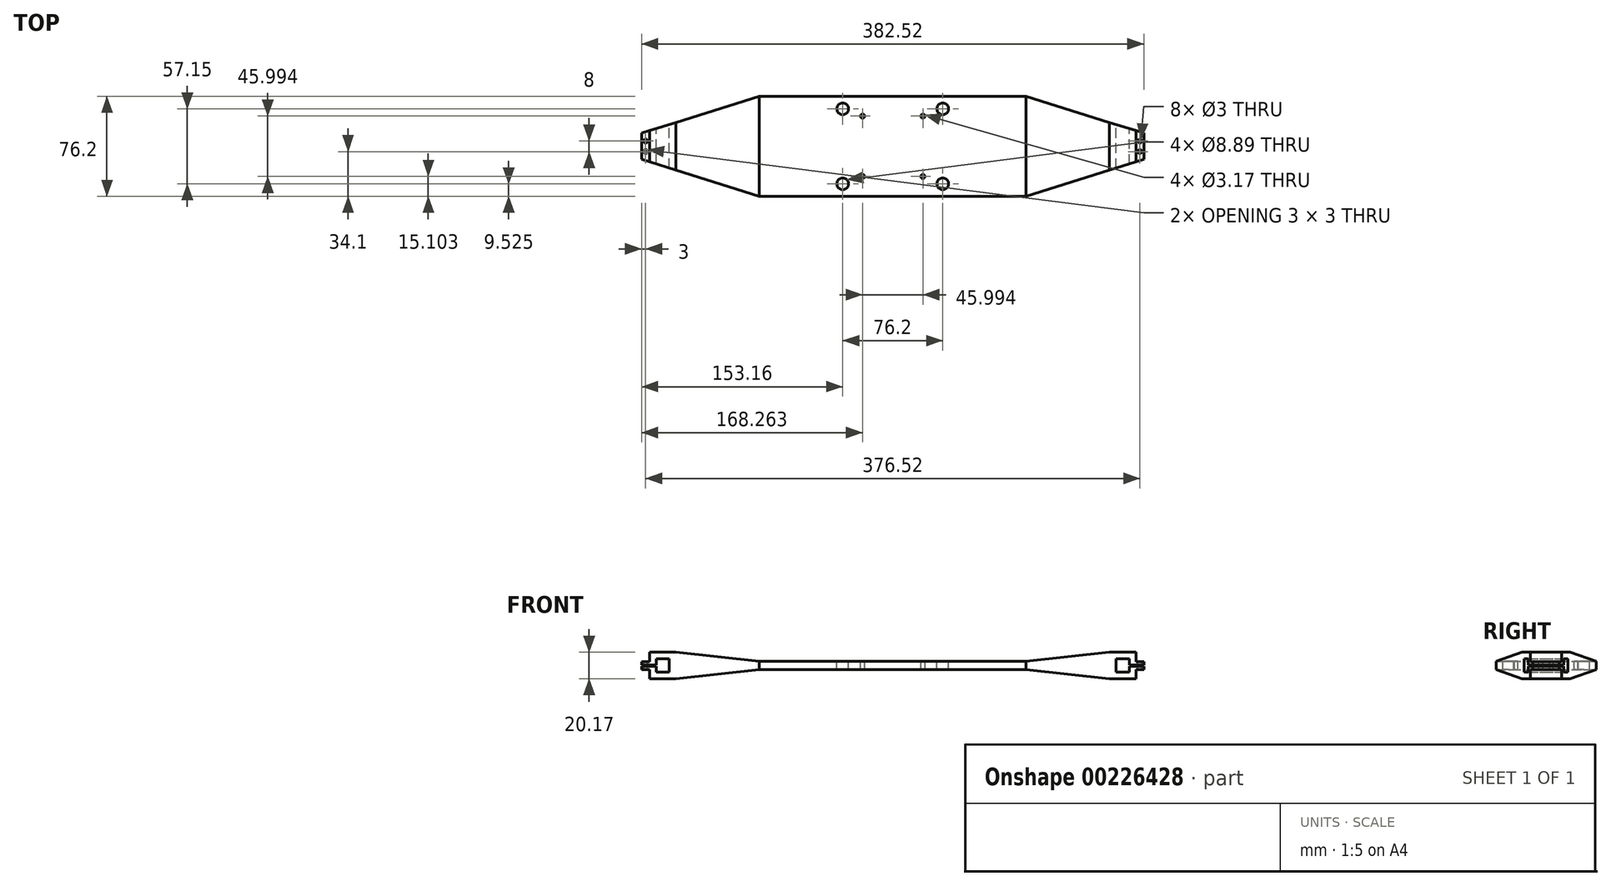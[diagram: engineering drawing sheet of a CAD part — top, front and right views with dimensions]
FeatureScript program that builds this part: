
annotation { "Feature Type Name" : "Feature", "Feature Type Description" : "" }
export const myFeature = defineFeature(function(context is Context, id is Id, definition is map)
    precondition{}
    {
        {
            var Q0;
            Q0=qCreatedBy(makeId("Front.planeOp"),FACE);
            var sketch = newSketch(context, id + "F0", { "sketchPlane" : qUnion([Q0])});
            skLineSegment(sketch, "E0.bottom", {"start": v(-180.18, 8.18) * mm, "end": v(-170.18, 8.18) * mm});
            skLineSegment(sketch, "E0.top", {"start": v(-180.18, -1.83) * mm, "end": v(-170.18, -1.83) * mm});
            skLineSegment(sketch, "E0.right", {"start": v(-170.18, 8.18) * mm, "end": v(-170.18, -1.83) * mm});
            skLineSegment(sketch, "E1.bottom", {"start": v(-165.1, -6.9) * mm, "end": v(-185.26, -6.9) * mm});
            skLineSegment(sketch, "E1.top", {"start": v(-165.1, 13.25) * mm, "end": v(-185.26, 13.25) * mm});
            skLineSegment(sketch, "E1.left", {"start": v(-165.1, -6.9) * mm, "end": v(-165.1, 13.25) * mm});
            skLineSegment(sketch, "E1.right", {"start": v(-185.26, -6.9) * mm, "end": v(-185.26, 2.68) * mm});
            skPoint(sketch, "E1.middle", {"position": v(-175.18, 3.17) * mm});
            skLineSegment(sketch, "E2", {"start": v(-185.26, 13.25) * mm, "end": v(-180.18, 8.17) * mm, "construction": true});
            skLineSegment(sketch, "E3", {"start": v(-170.18, -1.83) * mm, "end": v(-165.1, -6.9) * mm, "construction": true});
            skLineSegment(sketch, "E4", {"start": v(-180.18, -1.82) * mm, "end": v(-185.26, -6.9) * mm, "construction": true});
            skLineSegment(sketch, "E5", {"start": v(-165.1, 6.35) * mm, "end": v(0, 6.35) * mm});
            skLineSegment(sketch, "E6", {"start": v(0, 0) * mm, "end": v(-165.1, 0) * mm});
            skLineSegment(sketch, "E7", {"start": v(-165.1, 13.25) * mm, "end": v(-101.6, 6.35) * mm});
            skLineSegment(sketch, "E8", {"start": v(-101.6, 6.35) * mm, "end": v(-101.6, 0) * mm});
            skLineSegment(sketch, "E9", {"start": v(-101.6, 0) * mm, "end": v(-165.1, -6.9) * mm});
            skLineSegment(sketch, "E10", {"start": v(0, 6.35) * mm, "end": v(0, 0) * mm});
            skLineSegment(sketch, "E11", {"start": v(-180.18, 3.68) * mm, "end": v(-185.26, 3.68) * mm});
            skLineSegment(sketch, "E12", {"start": v(-185.26, 2.68) * mm, "end": v(-180.18, 2.68) * mm});
            skPoint(sketch, "E13", {"position": v(-180.18, 3.17) * mm});
            skLineSegment(sketch, "E14.trimOffspring", {"start": v(-180.18, 2.68) * mm, "end": v(-180.18, -1.83) * mm});
            skLineSegment(sketch, "E15", {"start": v(-180.18, 3.67) * mm, "end": v(-180.18, 8.17) * mm});
            skLineSegment(sketch, "E16.trimOffspring", {"start": v(-185.26, 3.67) * mm, "end": v(-185.26, 13.25) * mm});
            skLineSegment(sketch, "E17", {"start": v(-185.26, 3.68) * mm, "end": v(-191.26, 3.68) * mm});
            skLineSegment(sketch, "E18", {"start": v(-191.26, 3.67) * mm, "end": v(-191.26, 6.22) * mm});
            skLineSegment(sketch, "E19", {"start": v(-191.26, 6.22) * mm, "end": v(-185.26, 6.22) * mm});
            skLineSegment(sketch, "E20", {"start": v(-185.26, 2.68) * mm, "end": v(-191.26, 2.68) * mm});
            skLineSegment(sketch, "E21", {"start": v(-191.26, 2.68) * mm, "end": v(-191.26, 0.13) * mm});
            skLineSegment(sketch, "E22", {"start": v(-191.26, 0.13) * mm, "end": v(-185.26, 0.13) * mm});
            skLineSegment(sketch, "E23.MirrorCS", {"start": v(180.18, 3.67) * mm, "end": v(180.18, 8.17) * mm});
            skLineSegment(sketch, "E24.MirrorCS", {"start": v(180.18, 2.68) * mm, "end": v(180.18, -1.83) * mm});
            skLineSegment(sketch, "E25.MirrorCS", {"start": v(191.26, 3.67) * mm, "end": v(191.26, 6.22) * mm});
            skLineSegment(sketch, "E26.MirrorCS", {"start": v(191.26, 2.67) * mm, "end": v(191.26, 0.13) * mm});
            skLineSegment(sketch, "E27.MirrorCS", {"start": v(180.18, 8.18) * mm, "end": v(170.18, 8.18) * mm});
            skLineSegment(sketch, "E28.MirrorCS", {"start": v(180.18, 3.68) * mm, "end": v(185.26, 3.68) * mm});
            skLineSegment(sketch, "E29.MirrorCS", {"start": v(185.26, 2.68) * mm, "end": v(180.18, 2.68) * mm});
            skLineSegment(sketch, "E30.MirrorCS", {"start": v(180.18, -1.82) * mm, "end": v(185.26, -6.9) * mm, "construction": true});
            skLineSegment(sketch, "E31.MirrorCS", {"start": v(185.26, 13.25) * mm, "end": v(180.18, 8.17) * mm, "construction": true});
            skLineSegment(sketch, "E32.MirrorCS", {"start": v(191.26, 6.22) * mm, "end": v(185.26, 6.22) * mm});
            skLineSegment(sketch, "E33.MirrorCS", {"start": v(185.26, -6.9) * mm, "end": v(185.26, 2.68) * mm});
            skLineSegment(sketch, "E34.MirrorCS", {"start": v(191.26, 0.13) * mm, "end": v(185.26, 0.13) * mm});
            skLineSegment(sketch, "E35.MirrorCS", {"start": v(170.18, 8.18) * mm, "end": v(170.18, -1.82) * mm});
            skLineSegment(sketch, "E36.MirrorCS", {"start": v(0, 0) * mm, "end": v(165.1, 0) * mm});
            skLineSegment(sketch, "E37.MirrorCS", {"start": v(180.18, -1.83) * mm, "end": v(170.18, -1.83) * mm});
            skPoint(sketch, "E38.MirrorP", {"position": v(175.18, 3.17) * mm});
            skPoint(sketch, "E39.MirrorP", {"position": v(180.18, 3.17) * mm});
            skLineSegment(sketch, "E40.MirrorCS", {"start": v(101.6, 6.35) * mm, "end": v(101.6, 0) * mm});
            skLineSegment(sketch, "E41.MirrorCS", {"start": v(165.1, 13.25) * mm, "end": v(185.26, 13.25) * mm});
            skLineSegment(sketch, "E42.MirrorCS", {"start": v(165.1, -6.9) * mm, "end": v(185.26, -6.9) * mm});
            skLineSegment(sketch, "E43.MirrorCS", {"start": v(185.26, 3.67) * mm, "end": v(185.26, 13.25) * mm});
            skLineSegment(sketch, "E44.MirrorCS", {"start": v(165.1, -6.9) * mm, "end": v(165.1, 13.25) * mm});
            skLineSegment(sketch, "E45.MirrorCS", {"start": v(165.1, 6.35) * mm, "end": v(0, 6.35) * mm});
            skLineSegment(sketch, "E46.MirrorCS", {"start": v(185.26, 3.68) * mm, "end": v(191.26, 3.68) * mm});
            skLineSegment(sketch, "E47.MirrorCS", {"start": v(101.6, 0) * mm, "end": v(165.1, -6.9) * mm});
            skLineSegment(sketch, "E48.MirrorCS", {"start": v(185.26, 2.68) * mm, "end": v(191.26, 2.68) * mm});
            skLineSegment(sketch, "E49.MirrorCS", {"start": v(170.18, -1.83) * mm, "end": v(165.1, -6.9) * mm, "construction": true});
            skLineSegment(sketch, "E50.MirrorCS", {"start": v(165.1, 13.25) * mm, "end": v(101.6, 6.35) * mm});
            skSolve(sketch);
        }
        {
            var Q0;
            Q0 = qSketchRegion(id + "F0", true);
            extrude(context, id + "F1", {"entities" : qUnion([Q0]), "depth" : 76.2 * mm, "offsetDistance" : 25.4 * mm});
        }
        {
            var Q0;
            Q0=makeQuery(id+"F1.opExtrude","SWEPT_FACE",FACE,{"disambiguationData":[OSD([sQuery(id+"F0.wireOp",EDGE,"E5")])]});
            var sketch = newSketch(context, id + "F2", { "sketchPlane" : qUnion([Q0])});
            skLineSegment(sketch, "E51.bottom", {"start": v(-101.6, 0) * mm, "end": v(101.6, 0) * mm, "construction": true});
            skLineSegment(sketch, "E51.top", {"start": v(-101.6, -76.2) * mm, "end": v(101.6, -76.2) * mm, "construction": true});
            skLineSegment(sketch, "E51.left", {"start": v(-101.6, 0) * mm, "end": v(-101.6, -76.2) * mm, "construction": true});
            skLineSegment(sketch, "E51.right", {"start": v(101.6, 0) * mm, "end": v(101.6, -76.2) * mm, "construction": true});
            skLineSegment(sketch, "E52.bottom", {"start": v(-26, -12.1) * mm, "end": v(26, -12.1) * mm, "construction": true});
            skLineSegment(sketch, "E52.top", {"start": v(-26, -64.1) * mm, "end": v(26, -64.1) * mm, "construction": true});
            skLineSegment(sketch, "E52.left", {"start": v(-26, -12.1) * mm, "end": v(-26, -64.1) * mm, "construction": true});
            skLineSegment(sketch, "E52.right", {"start": v(26, -12.1) * mm, "end": v(26, -64.1) * mm, "construction": true});
            skLineSegment(sketch, "E53.bottom", {"start": v(-38.1, -9.52) * mm, "end": v(38.1, -9.52) * mm, "construction": true});
            skLineSegment(sketch, "E53.top", {"start": v(-38.1, -66.68) * mm, "end": v(38.1, -66.68) * mm, "construction": true});
            skLineSegment(sketch, "E53.left", {"start": v(-38.1, -9.52) * mm, "end": v(-38.1, -66.67) * mm, "construction": true});
            skLineSegment(sketch, "E53.right", {"start": v(38.1, -9.52) * mm, "end": v(38.1, -66.67) * mm, "construction": true});
            skLineSegment(sketch, "E54", {"start": v(0, -12.1) * mm, "end": v(0, 0) * mm, "construction": true});
            skLineSegment(sketch, "E55", {"start": v(26, -38.1) * mm, "end": v(101.6, -38.1) * mm, "construction": true});
            skLineSegment(sketch, "E56", {"start": v(0, -9.52) * mm, "end": v(0, 0) * mm});
            skLineSegment(sketch, "E57", {"start": v(38.1, -38.1) * mm, "end": v(101.6, -38.1) * mm, "construction": true});
            skCircle(sketch, "E58", {"center": v(-38.1, -9.52) * mm, "radius": 4.45 * mm});
            skCircle(sketch, "E59", {"center": v(38.1, -9.52) * mm, "radius": 4.45 * mm});
            skCircle(sketch, "E60", {"center": v(38.1, -66.67) * mm, "radius": 4.45 * mm});
            skCircle(sketch, "E61", {"center": v(-38.1, -66.67) * mm, "radius": 4.45 * mm});
            skCircle(sketch, "E62", {"center": v(-23, -15.1) * mm, "radius": 1.59 * mm});
            skCircle(sketch, "E63", {"center": v(23, -61.1) * mm, "radius": 1.59 * mm});
            skLineSegment(sketch, "E64", {"start": v(-23, -12.1) * mm, "end": v(-23, -64.1) * mm, "construction": true});
            skLineSegment(sketch, "E65", {"start": v(-26, -61.1) * mm, "end": v(26, -61.1) * mm, "construction": true});
            skLineSegment(sketch, "E66", {"start": v(23, -64.1) * mm, "end": v(23, -12.1) * mm, "construction": true});
            skLineSegment(sketch, "E67", {"start": v(26, -15.1) * mm, "end": v(-26, -15.1) * mm, "construction": true});
            skCircle(sketch, "E68", {"center": v(23, -15.1) * mm, "radius": 1.59 * mm});
            skCircle(sketch, "E69", {"center": v(-23, -61.1) * mm, "radius": 1.59 * mm});
            skSolve(sketch);
        }
        {
            var Q0;
            Q0 = qSketchRegion(id + "F2", true);
            extrude(context, id + "F3", {"entities" : qUnion([Q0]), "operationType" : NewBodyOperationType.REMOVE, "oppositeDirection" : true, "depth" : 25.4 * mm, "offsetDistance" : 25.4 * mm});
        }
        {
            var Q0;
            Q0=makeQuery(id+"F1.opExtrude","SWEPT_FACE",FACE,{"disambiguationData":[OSD([sQuery(id+"F0.wireOp",EDGE,"E19")])]});
            var sketch = newSketch(context, id + "F4", { "sketchPlane" : qUnion([Q0])});
            skCircle(sketch, "E70", {"center": v(-188.26, -34.1) * mm, "radius": 1.5 * mm});
            skPoint(sketch, "E70.centerSnap0", {"position": v(-188.26, 0) * mm});
            skCircle(sketch, "E71", {"center": v(-188.26, -42.1) * mm, "radius": 1.5 * mm});
            skPoint(sketch, "E71.centerSnap0", {"position": v(-188.26, -76.2) * mm});
            skLineSegment(sketch, "E72", {"start": v(0, 0) * mm, "end": v(0, -76.82) * mm});
            skCircle(sketch, "E73.MirrorC", {"center": v(188.26, -42.1) * mm, "radius": 1.5 * mm});
            skCircle(sketch, "E74.MirrorC", {"center": v(188.26, -34.1) * mm, "radius": 1.5 * mm});
            skPoint(sketch, "E75.MirrorP", {"position": v(188.26, -76.2) * mm});
            skSolve(sketch);
        }
        {
            var Q0;
            Q0 = qSketchRegion(id + "F4", true);
            extrude(context, id + "F5", {"entities" : qUnion([Q0]), "operationType" : NewBodyOperationType.REMOVE, "endBound" : BoundingType.THROUGH_ALL, "oppositeDirection" : true, "depth" : 25 * mm, "offsetDistance" : 25 * mm});
        }
        {
            var Q0;
            Q0=makeQuery(id+"F1.opExtrude","SWEPT_FACE",FACE,{"disambiguationData":[OSD([sQuery(id+"F0.wireOp",EDGE,"E1.top")])]});
            var sketch = newSketch(context, id + "F6", { "sketchPlane" : qUnion([Q0])});
            skPoint(sketch, "E76.0", {"position": v(-101.6, 0) * mm});
            skLineSegment(sketch, "E77", {"start": v(-101.6, 0) * mm, "end": v(-191.26, -28.1) * mm});
            skLineSegment(sketch, "E78.0", {"start": v(-191.26, -76.2) * mm, "end": v(-191.26, 0) * mm});
            skPoint(sketch, "E79", {"position": v(-191.26, -38.1) * mm});
            skLineSegment(sketch, "E80.MirrorCS", {"start": v(101.6, 0) * mm, "end": v(191.26, -28.1) * mm});
            skLineSegment(sketch, "E81", {"start": v(-191.26, -38.1) * mm, "end": v(196.24, -38.1) * mm});
            skLineSegment(sketch, "E82.MirrorCS", {"start": v(-101.6, -76.2) * mm, "end": v(-191.26, -48.1) * mm});
            skLineSegment(sketch, "E83.MirrorCS", {"start": v(101.6, -76.2) * mm, "end": v(191.26, -48.1) * mm});
            skLineSegment(sketch, "E84", {"start": v(-101.6, 0) * mm, "end": v(-191.26, 0) * mm});
            skLineSegment(sketch, "E85", {"start": v(-101.6, -76.2) * mm, "end": v(-191.26, -76.2) * mm});
            skLineSegment(sketch, "E86", {"start": v(101.6, -76.2) * mm, "end": v(191.26, -76.2) * mm});
            skLineSegment(sketch, "E87", {"start": v(191.26, -76.2) * mm, "end": v(191.26, -48.1) * mm});
            skLineSegment(sketch, "E88", {"start": v(191.26, -28.1) * mm, "end": v(191.26, 0) * mm});
            skLineSegment(sketch, "E89", {"start": v(191.26, 0) * mm, "end": v(101.6, 0) * mm});
            skSolve(sketch);
        }
        {
            var Q0;
            {var subQ0=sQuery(id+"F6.wireOp",EDGE,"E84");var subQ1=sQuery(id+"F6.wireOp",EDGE,"E77");var subQ2=makeQuery(id+"F6.imprint","INTERSECT",VERTEX,{"derivedFrom":[subQ1,subQ0]});Q0=makeQuery(id+"F6.imprint","IMPRINT",FACE,{"disambiguationData":[TD([[makeQuery(id+"F6.imprint","IMPRINT",EDGE,{"disambiguationData":[TD([[subQ2,-1.0]])],"derivedFrom":subQ1}),-1.0]])]});}
            var Q1;
            {var subQ0=sQuery(id+"F6.wireOp",EDGE,"E77");var subQ1=sQuery(id+"F0.wireOp",EDGE,"E1.top");var subQ4=makeQuery(id+"F1.opExtrude","SWEPT_EDGE",EDGE,{"disambiguationData":[OSD([subQ1,sQuery(id+"F0.wireOp",EDGE,"E16.trimOffspring")])]});var subQ5=makeQuery(id+"F6.imprint","INTERSECT",VERTEX,{"derivedFrom":[subQ4,subQ0]});Q1=makeQuery(id+"F6.imprint","IMPRINT",FACE,{"disambiguationData":[TD([[makeQuery(id+"F6.imprint","IMPRINT",EDGE,{"disambiguationData":[TD([[subQ5,1.0]])],"derivedFrom":subQ0}),-1.0]])]});}
            var Q2;
            {var subQ0=sQuery(id+"F6.wireOp",EDGE,"E78.0");var subQ1=sQuery(id+"F6.wireOp",EDGE,"E77");var subQ2=makeQuery(id+"F6.imprint","INTERSECT",VERTEX,{"derivedFrom":[subQ1,subQ0]});Q2=makeQuery(id+"F6.imprint","IMPRINT",FACE,{"disambiguationData":[TD([[makeQuery(id+"F6.imprint","IMPRINT",EDGE,{"disambiguationData":[TD([[subQ2,-1.0]])],"derivedFrom":subQ0}),-1.0]])]});}
            var Q3;
            {var subQ0=sQuery(id+"F6.wireOp",EDGE,"E85");var subQ1=sQuery(id+"F6.wireOp",EDGE,"E78.0");var subQ2=makeQuery(id+"F6.imprint","INTERSECT",VERTEX,{"derivedFrom":[subQ1,subQ0]});Q3=makeQuery(id+"F6.imprint","IMPRINT",FACE,{"disambiguationData":[TD([[makeQuery(id+"F6.imprint","IMPRINT",EDGE,{"disambiguationData":[TD([[subQ2,-1.0]])],"derivedFrom":subQ1}),-1.0]])]});}
            var Q4;
            {var subQ0=sQuery(id+"F6.wireOp",EDGE,"E82.MirrorCS");var subQ1=sQuery(id+"F0.wireOp",EDGE,"E1.top");var subQ4=makeQuery(id+"F1.opExtrude","SWEPT_EDGE",EDGE,{"disambiguationData":[OSD([subQ1,sQuery(id+"F0.wireOp",EDGE,"E16.trimOffspring")])]});var subQ5=makeQuery(id+"F6.imprint","INTERSECT",VERTEX,{"derivedFrom":[subQ4,subQ0]});Q4=makeQuery(id+"F6.imprint","IMPRINT",FACE,{"disambiguationData":[TD([[makeQuery(id+"F6.imprint","IMPRINT",EDGE,{"disambiguationData":[TD([[subQ5,1.0]])],"derivedFrom":subQ0}),1.0]])]});}
            var Q5;
            {var subQ0=sQuery(id+"F6.wireOp",EDGE,"E85");var subQ1=sQuery(id+"F6.wireOp",EDGE,"E82.MirrorCS");var subQ2=makeQuery(id+"F6.imprint","INTERSECT",VERTEX,{"derivedFrom":[subQ1,subQ0]});Q5=makeQuery(id+"F6.imprint","IMPRINT",FACE,{"disambiguationData":[TD([[makeQuery(id+"F6.imprint","IMPRINT",EDGE,{"disambiguationData":[TD([[subQ2,-1.0]])],"derivedFrom":subQ1}),1.0]])]});}
            var Q6;
            Q6=makeQuery(id+"F6.imprint","IMPRINT",FACE,{"disambiguationData":[TD([[makeQuery(id+"F6.imprint","IMPRINT",EDGE,{"derivedFrom":sQuery(id+"F6.wireOp",EDGE,"E83.MirrorCS")}),-1.0]])]});
            var Q7;
            Q7=makeQuery(id+"F6.imprint","IMPRINT",FACE,{"disambiguationData":[TD([[makeQuery(id+"F6.imprint","IMPRINT",EDGE,{"derivedFrom":sQuery(id+"F6.wireOp",EDGE,"E80.MirrorCS")}),1.0]])]});
            extrude(context, id + "F7", {"entities" : qUnion([Q0, Q1, Q2, Q3, Q4, Q5, Q6, Q7]), "operationType" : NewBodyOperationType.REMOVE, "endBound" : BoundingType.THROUGH_ALL, "oppositeDirection" : true, "depth" : 25 * mm, "offsetDistance" : 25 * mm});
        }
    });
